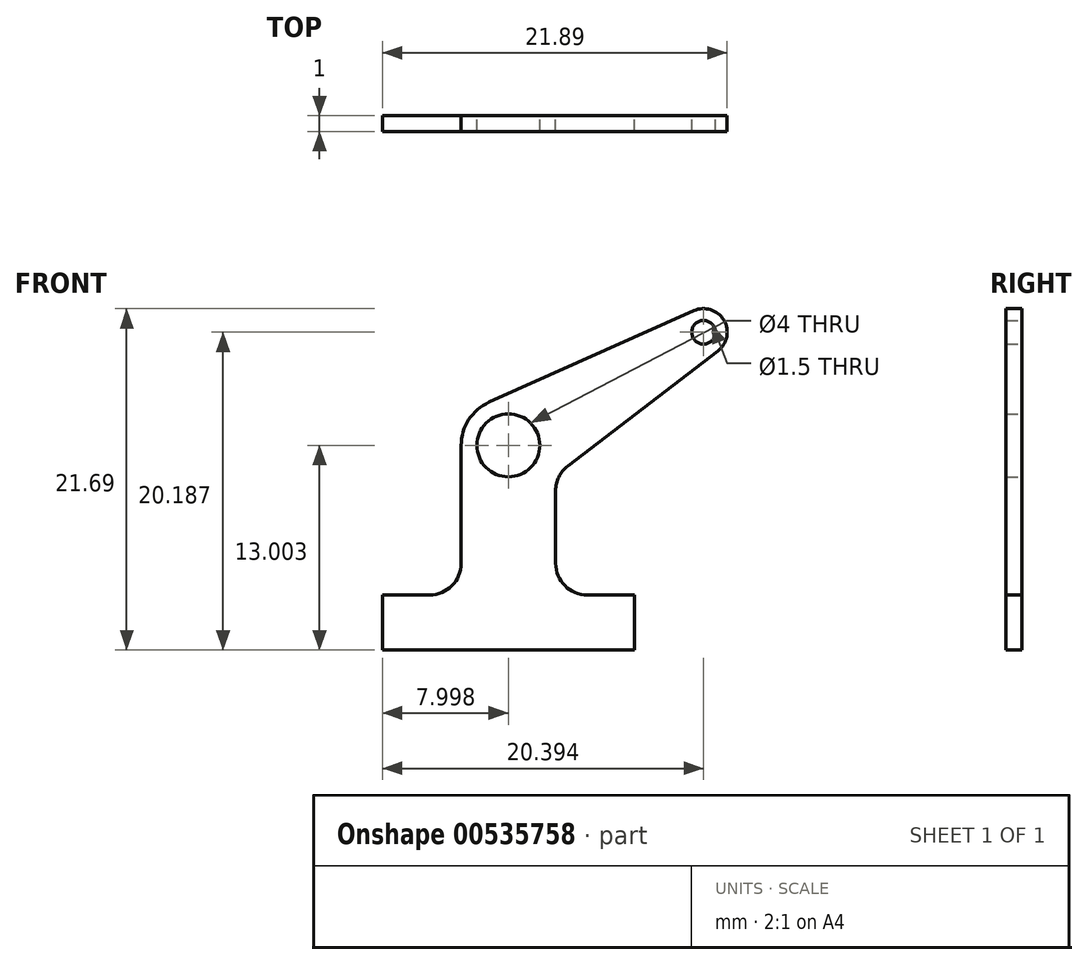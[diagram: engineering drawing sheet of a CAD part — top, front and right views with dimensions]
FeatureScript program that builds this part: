
annotation { "Feature Type Name" : "Feature", "Feature Type Description" : "" }
export const myFeature = defineFeature(function(context is Context, id is Id, definition is map)
    precondition{}
    {
        {
            var Q0;
            Q0=qCreatedBy(makeId("Front.planeOp"),FACE);
            var sketch = newSketch(context, id + "F0", { "sketchPlane" : qUnion([Q0])});
            skCircle(sketch, "E0", {"center": v(-2.55, 4.51) * mm, "radius": 2 * mm});
            skArc(sketch, "E1", {"start": v(-3.78, 7.25) * mm, "mid": v(-5.07, 6.14) * mm, "end": v(-5.55, 4.51) * mm});
            skArc(sketch, "E2", {"start": v(10.76, 10.5) * mm, "mid": v(11.13, 12.46) * mm, "end": v(9.23, 13.07) * mm});
            skCircle(sketch, "E3", {"center": v(9.84, 11.7) * mm, "radius": 0.75 * mm});
            skLineSegment(sketch, "E4", {"start": v(-10.55, -8.49) * mm, "end": v(5.45, -8.49) * mm});
            skLineSegment(sketch, "E5", {"start": v(5.45, -8.49) * mm, "end": v(5.45, -4.99) * mm});
            skLineSegment(sketch, "E6", {"start": v(-7.55, -4.99) * mm, "end": v(-10.55, -4.99) * mm});
            skLineSegment(sketch, "E7", {"start": v(-10.55, -4.99) * mm, "end": v(-10.55, -8.49) * mm});
            skLineSegment(sketch, "E8", {"start": v(-5.55, -2.99) * mm, "end": v(-5.55, 4.51) * mm});
            skLineSegment(sketch, "E9", {"start": v(0.45, 1.62) * mm, "end": v(0.45, -2.99) * mm});
            skArc(sketch, "E10.filletArc", {"start": v(-7.55, -4.99) * mm, "mid": v(-6.14, -4.4) * mm, "end": v(-5.55, -2.99) * mm});
            skLineSegment(sketch, "E11", {"start": v(5.45, -4.99) * mm, "end": v(2.45, -4.99) * mm});
            skPoint(sketch, "E12.visualSharp", {"position": v(0.45, -4.99) * mm});
            skArc(sketch, "E12.filletArc", {"start": v(0.45, -2.99) * mm, "mid": v(1.03, -4.4) * mm, "end": v(2.45, -4.99) * mm});
            skLineSegment(sketch, "E13", {"start": v(1.23, 3.21) * mm, "end": v(10.76, 10.5) * mm});
            skLineSegment(sketch, "E14", {"start": v(9.23, 13.07) * mm, "end": v(-3.78, 7.25) * mm});
            skArc(sketch, "E15.filletArc", {"start": v(1.23, 3.21) * mm, "mid": v(0.65, 2.5) * mm, "end": v(0.45, 1.62) * mm});
            skSolve(sketch);
        }
        {
            var Q0;
            Q0 = qSketchRegion(id + "F0", true);
            extrude(context, id + "F1", {"entities" : qUnion([Q0]), "endBound" : BoundingType.SYMMETRIC, "depth" : 1 * mm, "offsetDistance" : 25 * mm});
        }
    });
